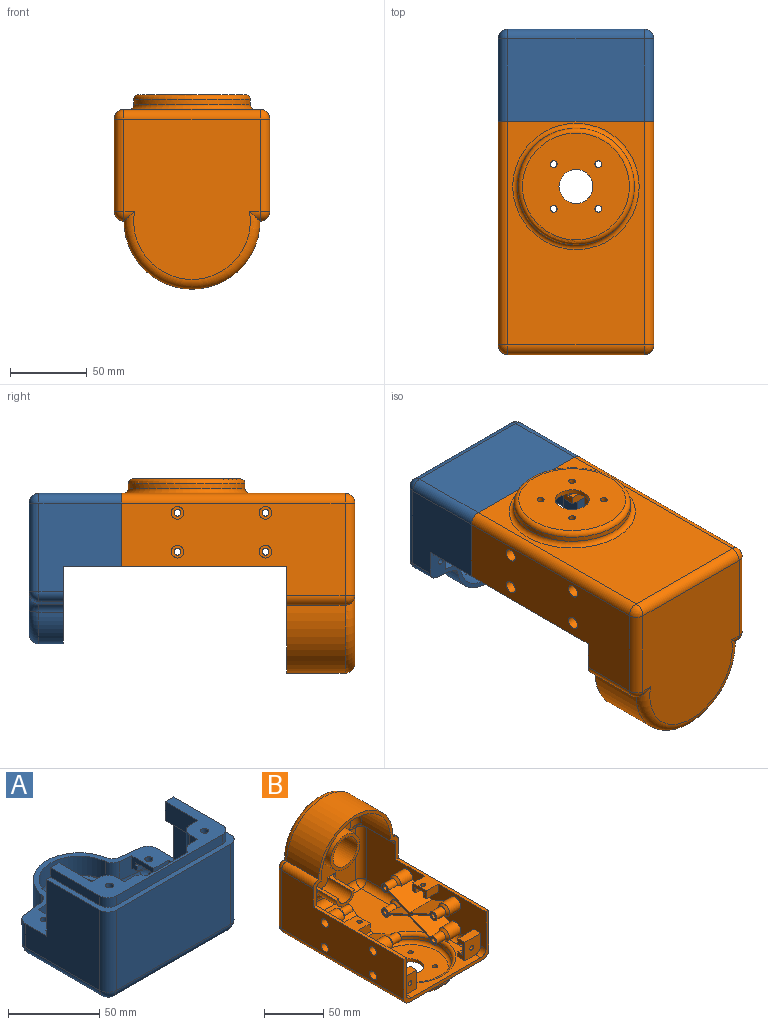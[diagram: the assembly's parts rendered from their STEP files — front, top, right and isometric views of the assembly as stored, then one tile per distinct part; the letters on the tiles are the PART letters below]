
ASSEMBLY  parts=2 mates=1
PART A: 121 faces, bbox 101.6x103.7x66.7 mm
  f0: plane 25.4x12.7mm, normal (1,0,0), area 322.6mm2, adj f10,f30,f31,f37
  f1: plane 12.7x6.55mm, normal (0,1,0), area 83.2mm2, adj f19,f31,f36,f119
  f2: plane 44.45x32.87mm, normal (-1,0,0), area 939.6mm2, adj f11,f20,f47,f58,f59,f103,f109,f112
  f3: plane 44.45x32.87mm, normal (1,0,0), area 939.6mm2, adj f10,f30,f47,f48,f51,f94,f99,f100
  f4: plane 8.89x1.27mm, normal (0,0,1), area 11.3mm2, adj f54,f56,f57,f62
  f5: plane 8.89x1.27mm, normal (0,0,1), area 11.3mm2, adj f54,f55,f56,f63
  f6: plane 8.89x1.27mm, normal (0,0,1), area 11.3mm2, adj f49,f50,f53,f60
  f7: plane 8.89x1.27mm, normal (0,0,1), area 11.3mm2, adj f50,f52,f53,f61
  f8: plane 14.41x12.7mm, normal (-0.12,-0.99,0), area 135.7mm2, adj f47,f54,f59,f110,f112,f117
  f9: plane 14.41x12.7mm, normal (0.12,-0.99,0), area 135.7mm2, adj f47,f48,f50,f100,f105,f115
  f10: plane 44.45x9.53mm, normal (0,1,0), area 201.6mm2, adj f0,f3,f12,f26,f28,f30,f31,f47
  f11: plane 44.45x9.53mm, normal (0,1,0), area 201.6mm2, adj f2,f15,f20,f26,f31,f32,f34,f47
  f12: plane 57.89x53.98mm, normal (-1,0,0), area 2491.7mm2, adj f10,f26,f47,f75,f81,f82
  f13: plane 82.55x54.33mm, normal (0,0,1), area 3316.7mm2, adj f87,f90,f92,f93,f98,f99,f101,f104
  f14: plane 88.9x85.73mm, normal (0,0,-1), area 6067.7mm2, adj f40,f42,f70,f73,f76,f77,f79,f82
  f15: plane 57.89x53.98mm, normal (1,0,0), area 2491.7mm2, adj f11,f26,f47,f68,f69,f70
  f16: cylinder r=2.22mm len=15.88mm, axis (0,0,1), area 221.7mm2, adj f31,f41
  f17: cylinder r=2.22mm len=15.88mm, axis (0,0,1), area 221.7mm2, adj f31,f39
  f18: plane 44.45x44.45mm, normal (0,1,0), area 1975.8mm2, adj f19,f86,f91,f92
  f19: plane 57.15x6.35mm, normal (0,0,-1), area 179.2mm2, adj f1,f18,f21,f33,f86,f91,f119,f120
  f20: plane 25.4x6.35mm, normal (0,0,-1), area 152.6mm2, adj f2,f11,f34,f103
  f21: plane 12.7x6.55mm, normal (0,1,0), area 83.2mm2, adj f19,f31,f38,f120
  f22: cylinder r=14.29mm len=28.58mm, axis (0,0,-1), area 855.1mm2, adj f24,f25
  f23: cylinder r=17.46mm len=34.93mm, axis (0,0,-1), area 348.4mm2, adj f24,f107
  f24: plane 34.93x34.93mm, normal (0,0,1), area 316.7mm2, adj f22,f23
  f25: plane 28.58x28.58mm, normal (0,0,1), area 641.3mm2, adj f22
  f26: plane 101.6x47.63mm, normal (0,0,1), area 604.8mm2, adj f10,f11,f12,f15,f27,f28,f29,f32
  f27: plane 88.9x53.98mm, normal (0,-1,0), area 4798.4mm2, adj f26,f69,f75,f76
  f28: plane 38.1x6.35mm, normal (-1,0,0), area 241.9mm2, adj f10,f26,f31,f114
  f29: plane 82.55x6.35mm, normal (0,-1,0), area 524.2mm2, adj f26,f31,f113,f114
  f30: plane 25.4x6.35mm, normal (0,0,-1), area 152.6mm2, adj f0,f3,f10,f94
  f31: plane 95.25x44.45mm, normal (0,0,1), area 1179.3mm2, adj f0,f1,f10,f11,f16,f17,f21,f28
  f32: plane 38.1x6.35mm, normal (1,0,0), area 241.9mm2, adj f11,f26,f31,f113
  f33: plane 31.75x12.7mm, normal (0,1,0), area 403.2mm2, adj f19,f31,f119,f120
  f34: plane 25.4x12.7mm, normal (-1,0,0), area 322.6mm2, adj f11,f20,f31,f35
  f35: plane 57.15x6.35mm, normal (0,1,0), area 362.9mm2, adj f31,f34,f97,f103,f104
  f36: plane 57.15x6.35mm, normal (-1,0,0), area 362.9mm2, adj f1,f31,f91,f97,f98
  f37: plane 57.15x6.35mm, normal (0,1,0), area 362.9mm2, adj f0,f31,f88,f93,f94
  f38: plane 57.15x6.35mm, normal (1,0,0), area 362.9mm2, adj f21,f31,f86,f87,f88
  f39: plane 8.26x8.26mm, normal (0,0,-1), area 38mm2, adj f17,f40
  f40: cylinder r=4.13mm len=50.8mm, axis (0,0,-1), area 1317.4mm2, adj f14,f39
  f41: plane 8.26x8.26mm, normal (0,0,-1), area 38mm2, adj f16,f42
  f42: cylinder r=4.13mm len=50.8mm, axis (0,0,-1), area 1317.4mm2, adj f14,f41
  f43: cylinder r=25.4mm len=49.98mm, axis (0,0,1), area 1122mm2, adj f47,f74,f79,f80
  f44: plane 15.88x14.79mm, normal (0.12,0.99,0), area 236.5mm2, adj f47,f68,f73,f74
  f45: plane 15.88x14.79mm, normal (-0.12,0.99,0), area 236.5mm2, adj f47,f80,f81,f85
  f46: cylinder r=22.23mm len=44.23mm, axis (0,0,-1), area 830.9mm2, adj f47,f108,f115,f117
  f47: plane 101.6x50.8mm, normal (0,0,1), area 868.3mm2, adj f2,f3,f8,f9,f10,f11,f12,f15
  f48: plane 17.04x11.43mm, normal (0,0,-1), area 101.1mm2, adj f3,f9,f49,f50,f51,f52,f53,f100
  f49: plane 8.89x3.3mm, normal (0,-1,0), area 29.4mm2, adj f6,f48,f50,f53
  f50: plane 17.04x8.26mm, normal (1,0,0), area 91mm2, adj f6,f7,f9,f47,f48,f49,f51,f52
  f51: plane 11.43x8.26mm, normal (0,-1,0), area 94.4mm2, adj f3,f47,f48,f50
  f52: plane 8.89x3.3mm, normal (0,1,0), area 29.4mm2, adj f7,f48,f50,f53
  f53: plane 11.43x5.08mm, normal (1,0,0), area 49.7mm2, adj f6,f7,f48,f49,f52,f60,f61,f65
  f54: plane 17.04x8.26mm, normal (-1,0,0), area 91mm2, adj f4,f5,f8,f47,f55,f57,f58,f59
  f55: plane 8.89x3.3mm, normal (0,-1,0), area 29.4mm2, adj f5,f54,f56,f59
  f56: plane 11.43x5.08mm, normal (-1,0,0), area 49.7mm2, adj f4,f5,f55,f57,f59,f62,f63,f67
  f57: plane 8.89x3.3mm, normal (0,1,0), area 29.4mm2, adj f4,f54,f56,f59
  f58: plane 11.43x8.26mm, normal (0,-1,0), area 94.4mm2, adj f2,f47,f54,f59
  f59: plane 17.04x11.43mm, normal (0,0,-1), area 101.1mm2, adj f2,f8,f54,f55,f56,f57,f58,f112
  f60: plane 8.89x1.78mm, normal (0,-1,0), area 15.8mm2, adj f6,f50,f53,f65
  f61: plane 8.89x1.78mm, normal (0,1,0), area 15.8mm2, adj f7,f50,f53,f65
  f62: plane 8.89x1.78mm, normal (0,1,0), area 15.8mm2, adj f4,f54,f56,f67
  f63: plane 8.89x1.78mm, normal (0,-1,0), area 15.8mm2, adj f5,f54,f56,f67
  f64: cylinder r=2.22mm len=4.45mm, axis (0,0,-1), area 44.3mm2, adj f47,f65
  f65: plane 11.43x8.89mm, normal (0,0,-1), area 86.1mm2, adj f50,f53,f60,f61,f64
  f66: cylinder r=2.22mm len=4.45mm, axis (0,0,-1), area 44.3mm2, adj f47,f67
  f67: plane 11.43x8.89mm, normal (0,0,-1), area 86.1mm2, adj f54,f56,f62,f63,f66
  f68: cylinder r=6.35mm len=15.88mm, axis (0,0,-1), area 145.8mm2, adj f15,f44,f47,f71
  f69: cylinder r=6.35mm len=53.98mm, axis (0,0,-1), area 538.4mm2, adj f15,f26,f27,f72
  f70: cylinder r=6.35mm len=57.89mm, axis (0,1,0), area 577.5mm2, adj f14,f15,f71,f72
  f71: sphere r=6.35mm, area 37.1mm2, adj f68,f70,f73
  f72: sphere r=6.35mm, area 63.3mm2, adj f69,f70,f76
  f73: cylinder r=6.35mm len=15.57mm, axis (0.99,-0.12,0), area 148.6mm2, adj f14,f44,f71,f77
  f74: cylinder r=6.35mm len=15.88mm, axis (0,0,1), area 127.7mm2, adj f43,f44,f47,f77
  f75: cylinder r=6.35mm len=53.98mm, axis (0,0,1), area 538.4mm2, adj f12,f26,f27,f78
  f76: cylinder r=6.35mm len=88.9mm, axis (-1,0,0), area 886.7mm2, adj f14,f27,f72,f78
  f77: torus R=12.7mm, axis (0,0,1), area 109.4mm2, adj f14,f73,f74,f79
  f78: sphere r=6.35mm, area 63.3mm2, adj f75,f76,f82
  f79: torus R=19.05mm, axis (0,0,1), area 640.9mm2, adj f14,f43,f77,f83
  f80: cylinder r=6.35mm len=15.88mm, axis (0,0,1), area 127.7mm2, adj f43,f45,f47,f83
  f81: cylinder r=6.35mm len=15.88mm, axis (0,0,-1), area 145.8mm2, adj f12,f45,f47,f84
  f82: cylinder r=6.35mm len=57.89mm, axis (0,-1,0), area 577.5mm2, adj f12,f14,f78,f84
  f83: torus R=12.7mm, axis (0,0,1), area 109.4mm2, adj f14,f79,f80,f85
  f84: sphere r=6.35mm, area 37.1mm2, adj f81,f82,f85
  f85: cylinder r=6.35mm len=15.57mm, axis (0.99,0.12,0), area 148.6mm2, adj f14,f45,f83,f84
  f86: cylinder r=6.35mm len=44.45mm, axis (0,0,1), area 443.4mm2, adj f18,f19,f38,f89
  f87: cylinder r=6.35mm len=6.35mm, axis (0,1,0), area 63.3mm2, adj f13,f38,f89,f90
  f88: cylinder r=6.35mm len=57.15mm, axis (0,0,1), area 570mm2, adj f31,f37,f38,f90
  f89: sphere r=6.35mm, area 63.3mm2, adj f86,f87,f92
  f90: torus R=12.7mm, axis (0,0,1), area 135.6mm2, adj f13,f87,f88,f93
  f91: cylinder r=6.35mm len=44.45mm, axis (0,0,-1), area 443.4mm2, adj f18,f19,f36,f95
  f92: cylinder r=6.35mm len=44.45mm, axis (1,0,0), area 443.4mm2, adj f13,f18,f89,f95
  f93: cylinder r=6.35mm len=6.35mm, axis (-1,0,0), area 63.3mm2, adj f13,f37,f90,f96
  f94: cylinder r=6.35mm len=44.45mm, axis (0,0,-1), area 443.4mm2, adj f3,f30,f37,f96
  f95: sphere r=6.35mm, area 40.3mm2, adj f91,f92,f98
  f96: sphere r=6.35mm, area 63.3mm2, adj f93,f94,f99
  f97: cylinder r=6.35mm len=57.15mm, axis (0,0,1), area 570mm2, adj f31,f35,f36,f101
  f98: cylinder r=6.35mm len=6.35mm, axis (0,-1,0), area 63.3mm2, adj f13,f36,f95,f101
  f99: cylinder r=6.35mm len=32.87mm, axis (0,1,0), area 327.8mm2, adj f3,f13,f96,f102
  f100: cylinder r=6.35mm len=6.3mm, axis (0,0,1), area 40.8mm2, adj f3,f9,f48,f102
  f101: torus R=12.7mm, axis (0,0,1), area 135.6mm2, adj f13,f97,f98,f104
  f102: sphere r=6.35mm, area 37.1mm2, adj f99,f100,f105
  f103: cylinder r=6.35mm len=44.45mm, axis (0,0,-1), area 443.4mm2, adj f2,f20,f35,f106
  f104: cylinder r=6.35mm len=6.35mm, axis (-1,0,0), area 63.3mm2, adj f13,f35,f101,f106
  f105: cylinder r=6.35mm len=22.09mm, axis (0.99,0.12,0), area 186mm2, adj f9,f13,f102,f107,f116
  f106: sphere r=6.35mm, area 86.4mm2, adj f103,f104,f109
  f107: torus R=23.81mm, axis (0,0,1), area 892.1mm2, adj f13,f23,f105,f108,f110,f116,f118
  f108: torus R=15.88mm, axis (0,0,1), area 370.4mm2, adj f46,f107,f116,f118
  f109: cylinder r=6.35mm len=32.87mm, axis (0,-1,0), area 327.8mm2, adj f2,f13,f106,f111
  f110: cylinder r=6.35mm len=22.09mm, axis (0.99,-0.12,0), area 186mm2, adj f8,f13,f107,f111,f118
  f111: sphere r=6.35mm, area 60.1mm2, adj f109,f110,f112
  f112: cylinder r=6.35mm len=6.3mm, axis (0,0,1), area 40.8mm2, adj f2,f8,f59,f111
  f113: cylinder r=6.35mm len=6.35mm, axis (0,0,-1), area 63.3mm2, adj f26,f29,f31,f32
  f114: cylinder r=6.35mm len=6.35mm, axis (0,0,1), area 63.3mm2, adj f26,f28,f29,f31
  f115: cylinder r=6.35mm len=12.7mm, axis (0,0,-1), area 108.7mm2, adj f9,f46,f47,f116
  f116: bspline ~9.93x8.8mm, area 52mm2, adj f105,f107,f108,f115
  f117: cylinder r=6.35mm len=12.7mm, axis (0,0,-1), area 108.7mm2, adj f8,f46,f47,f118
  f118: bspline ~10.23x8.96mm, area 52mm2, adj f107,f108,f110,f117
  f119: cylinder r=6.35mm len=12.7mm, axis (0,0,1), area 106.3mm2, adj f1,f19,f31,f33
  f120: cylinder r=6.35mm len=12.7mm, axis (0,0,1), area 106.3mm2, adj f19,f21,f31,f33
PART B: 195 faces, bbox 101.8x154.7x130.8 mm
  f0: cylinder r=2.22mm len=4.45mm, axis (0,0,1), area 44.3mm2, adj f187,f188
  f1: cylinder r=2.22mm len=4.45mm, axis (0,0,1), area 44.3mm2, adj f187,f188
  f2: cylinder r=2.22mm len=4.45mm, axis (0,0,1), area 44.3mm2, adj f187,f188
  f3: cylinder r=2.22mm len=4.45mm, axis (0,0,1), area 44.3mm2, adj f187,f188
  f4: cylinder r=11.11mm len=22.23mm, axis (0,0,-1), area 221.7mm2, adj f187,f188
  f5: plane 46.53x14.14mm, normal (-1,0,0), area 413.9mm2, adj f25,f30,f77,f79,f170
  f6: plane 142.88x53.98mm, normal (1,0,0), area 4724.8mm2, adj f9,f19,f38,f39,f41,f42,f43,f44
  f7: plane 19.05x8.26mm, normal (-1,0,0), area 107.6mm2, adj f17,f45,f105,f106,f109,f110,f115,f116
  f8: plane 11.43x5.08mm, normal (-1,0,0), area 49.7mm2, adj f17,f109,f110,f115,f116,f117,f118,f153
  f9: plane 19.05x8.26mm, normal (0,0,1), area 157.3mm2, adj f6,f102,f104,f152
  f10: plane 11.43x5.08mm, normal (1,0,0), area 49.7mm2, adj f103,f107,f108,f111,f112,f113,f114,f152
  f11: plane 46.53x14.14mm, normal (1,0,0), area 413.9mm2, adj f37,f40,f55,f56,f175
  f12: plane 142.88x53.98mm, normal (-1,0,0), area 4724.8mm2, adj f20,f26,f27,f28,f29,f31,f32,f70
  f13: plane 146.05x60.33mm, normal (-1,0,0), area 6539.9mm2, adj f19,f58,f60,f62,f64,f101,f125,f158
  f14: plane 104.78x88.9mm, normal (0,1,0), area 8124.7mm2, adj f156,f159,f162,f164,f165,f167
  f15: plane 146.05x60.33mm, normal (1,0,0), area 6539.9mm2, adj f20,f81,f83,f85,f87,f101,f125,f154
  f16: plane 98.43x82.55mm, normal (0,-1,0), area 4867.2mm2, adj f96,f97,f99,f169,f173,f174,f176,f178
  f17: plane 13.97x11.43mm, normal (0,1,0), area 144.2mm2, adj f7,f8,f109,f110,f119
  f18: plane 146.05x88.9mm, normal (0,0,-1), area 7631.7mm2, adj f101,f154,f158,f159,f192
  f19: plane 107.95x17.15mm, normal (0,0,1), area 557.9mm2, adj f6,f13,f101,f125,f126,f127,f129,f150
  f20: plane 107.95x17.15mm, normal (0,0,1), area 557.9mm2, adj f12,f15,f101,f125,f130,f132,f133,f151
  f21: cylinder r=2.22mm len=16.89mm, axis (1,0,0), area 235.9mm2, adj f75,f86
  f22: cylinder r=2.22mm len=16.89mm, axis (1,0,0), area 235.9mm2, adj f75,f84
  f23: cylinder r=2.22mm len=16.99mm, axis (1,0,0), area 237.3mm2, adj f82,f194
  f24: cylinder r=2.22mm len=16.89mm, axis (1,0,0), area 235.9mm2, adj f75,f80
  f25: plane 26.58x24.8mm, normal (0,0.4,-0.91), area 676.9mm2, adj f5,f30,f72,f75,f79,f91
  f26: plane 26.42x23.02mm, normal (0,-0.4,0.91), area 632mm2, adj f12,f72,f73,f75,f79,f91
  f27: plane 26.42x23.02mm, normal (0,-0.4,-0.91), area 632mm2, adj f12,f73,f74,f75,f78,f90
  f28: plane 26.58x24.8mm, normal (0,0.4,0.91), area 676.9mm2, adj f12,f32,f74,f75,f78,f90
  f29: plane 26.42x23.02mm, normal (0,0.4,0.91), area 632mm2, adj f12,f70,f71,f75,f77,f88
  f30: plane 26.58x24.8mm, normal (0,-0.4,-0.91), area 676.9mm2, adj f5,f25,f71,f75,f77,f88
  f31: plane 26.42x23.02mm, normal (0,0.4,-0.91), area 632mm2, adj f12,f69,f70,f75,f76,f89
  f32: plane 26.58x24.8mm, normal (0,-0.4,0.91), area 676.9mm2, adj f12,f28,f69,f75,f76,f89
  f33: cylinder r=2.22mm len=16.89mm, axis (1,0,0), area 235.9mm2, adj f52,f63
  f34: cylinder r=2.22mm len=16.89mm, axis (1,0,0), area 235.9mm2, adj f52,f61
  f35: cylinder r=2.22mm len=16.89mm, axis (1,0,0), area 235.9mm2, adj f52,f59
  f36: cylinder r=2.22mm len=16.89mm, axis (1,0,0), area 235.9mm2, adj f52,f57
  f37: plane 26.58x24.8mm, normal (0,-0.4,-0.91), area 676.9mm2, adj f11,f40,f51,f52,f56,f65
  f38: plane 26.42x23.02mm, normal (0,0.4,0.91), area 632mm2, adj f6,f46,f51,f52,f56,f65
  f39: plane 26.42x23.02mm, normal (0,-0.4,0.91), area 632mm2, adj f6,f49,f50,f52,f55,f66
  f40: plane 26.58x24.8mm, normal (0,0.4,-0.91), area 676.9mm2, adj f11,f37,f50,f52,f55,f66
  f41: plane 26.42x23.02mm, normal (0,0.4,-0.91), area 632mm2, adj f6,f46,f47,f52,f54,f68
  f42: plane 26.58x24.8mm, normal (0,-0.4,0.91), area 676.9mm2, adj f6,f43,f47,f52,f54,f68
  f43: plane 26.58x24.8mm, normal (0,0.4,0.91), area 676.9mm2, adj f6,f42,f48,f52,f53,f67
  f44: plane 26.42x23.02mm, normal (0,-0.4,-0.91), area 632mm2, adj f6,f48,f49,f52,f53,f67
  f45: plane 142.88x82.55mm, normal (0,0,1), area 7024.3mm2, adj f7,f101,f102,f104,f105,f152,f153,f170
  f46: plane 26.42x1.74mm, normal (0,1,0), area 45.8mm2, adj f6,f38,f41,f52
  f47: cylinder r=4.13mm len=10.54mm, axis (-1,0,0), area 256.2mm2, adj f41,f42,f52,f68
  f48: cylinder r=4.13mm len=10.54mm, axis (-1,0,0), area 256.2mm2, adj f43,f44,f52,f67
  f49: plane 26.42x1.74mm, normal (0,-1,0), area 45.8mm2, adj f6,f39,f44,f52
  f50: cylinder r=4.13mm len=10.54mm, axis (-1,0,0), area 256.2mm2, adj f39,f40,f52,f66
  f51: cylinder r=4.13mm len=10.54mm, axis (-1,0,0), area 256.2mm2, adj f37,f38,f52,f65
  f52: plane 65.79x33.66mm, normal (1,0,0), area 327.3mm2, adj f33,f34,f35,f36,f37,f38,f39,f40
  f53: cylinder r=6.35mm len=13.65mm, axis (-1,0,0), area 522.8mm2, adj f6,f43,f44,f67
  f54: cylinder r=6.35mm len=13.65mm, axis (-1,0,0), area 522.8mm2, adj f6,f41,f42,f68
  f55: cylinder r=6.35mm len=13.65mm, axis (-1,0,0), area 517mm2, adj f6,f11,f39,f40,f66,f175
  f56: cylinder r=6.35mm len=13.65mm, axis (-1,0,0), area 517mm2, adj f6,f11,f37,f38,f65,f175
  f57: plane 8.26x8.26mm, normal (-1,0,0), area 38mm2, adj f36,f58
  f58: cylinder r=4.13mm len=12.7mm, axis (-1,0,0), area 329.4mm2, adj f13,f57
  f59: plane 8.26x8.26mm, normal (-1,0,0), area 38mm2, adj f35,f60
  f60: cylinder r=4.13mm len=12.7mm, axis (-1,0,0), area 329.4mm2, adj f13,f59
  f61: plane 8.26x8.26mm, normal (-1,0,0), area 38mm2, adj f34,f62
  f62: cylinder r=4.13mm len=12.7mm, axis (-1,0,0), area 329.4mm2, adj f13,f61
  f63: plane 8.26x8.26mm, normal (-1,0,0), area 38mm2, adj f33,f64
  f64: cylinder r=4.13mm len=12.7mm, axis (-1,0,0), area 329.4mm2, adj f13,f63
  f65: cone r=4.13mm half-angle=45deg, axis (-1,0,0), area 98.2mm2, adj f37,f38,f51,f56
  f66: cone r=4.13mm half-angle=45deg, axis (-1,0,0), area 98.2mm2, adj f39,f40,f50,f55
  f67: cone r=4.13mm half-angle=45deg, axis (-1,0,0), area 98.2mm2, adj f43,f44,f48,f53
  f68: cone r=4.13mm half-angle=45deg, axis (-1,0,0), area 98.2mm2, adj f41,f42,f47,f54
  f69: cylinder r=4.13mm len=10.64mm, axis (1,0,0), area 258.8mm2, adj f31,f32,f75,f89,f194
  f70: plane 26.42x1.74mm, normal (0,1,0), area 45.8mm2, adj f12,f29,f31,f75
  f71: cylinder r=4.13mm len=10.54mm, axis (1,0,0), area 256.2mm2, adj f29,f30,f75,f88
  f72: cylinder r=4.13mm len=10.54mm, axis (1,0,0), area 256.2mm2, adj f25,f26,f75,f91
  f73: plane 26.42x1.74mm, normal (0,-1,0), area 45.8mm2, adj f12,f26,f27,f75
  f74: cylinder r=4.13mm len=10.54mm, axis (1,0,0), area 256.2mm2, adj f27,f28,f75,f90
  f75: plane 65.79x33.66mm, normal (-1,0,0), area 289.3mm2, adj f21,f22,f24,f25,f26,f27,f28,f29
  f76: cylinder r=6.35mm len=13.65mm, axis (1,0,0), area 522.8mm2, adj f12,f31,f32,f89
  f77: cylinder r=6.35mm len=13.65mm, axis (1,0,0), area 517mm2, adj f5,f12,f29,f30,f88,f170
  f78: cylinder r=6.35mm len=13.65mm, axis (1,0,0), area 522.8mm2, adj f12,f27,f28,f90
  f79: cylinder r=6.35mm len=13.65mm, axis (1,0,0), area 517mm2, adj f5,f12,f25,f26,f91,f170
  f80: plane 8.26x8.26mm, normal (1,0,0), area 38mm2, adj f24,f81
  f81: cylinder r=4.13mm len=12.7mm, axis (1,0,0), area 329.4mm2, adj f15,f80
  f82: plane 8.26x8.26mm, normal (1,0,0), area 38mm2, adj f23,f83
  f83: cylinder r=4.13mm len=12.7mm, axis (1,0,0), area 329.4mm2, adj f15,f82
  f84: plane 8.26x8.26mm, normal (1,0,0), area 38mm2, adj f22,f85
  f85: cylinder r=4.13mm len=12.7mm, axis (1,0,0), area 329.4mm2, adj f15,f84
  f86: plane 8.26x8.26mm, normal (1,0,0), area 38mm2, adj f21,f87
  f87: cylinder r=4.13mm len=12.7mm, axis (1,0,0), area 329.4mm2, adj f15,f86
  f88: cone r=4.13mm half-angle=45deg, axis (1,0,0), area 98.2mm2, adj f29,f30,f71,f77
  f89: cone r=4.13mm half-angle=45deg, axis (1,0,0), area 98.2mm2, adj f31,f32,f69,f76
  f90: cone r=4.13mm half-angle=45deg, axis (1,0,0), area 98.2mm2, adj f27,f28,f74,f78
  f91: cone r=4.13mm half-angle=45deg, axis (1,0,0), area 98.2mm2, adj f25,f26,f72,f79
  f92: cylinder r=14.29mm len=28.58mm, axis (0,1,0), area 2565.2mm2, adj f94,f95
  f93: cylinder r=17.46mm len=34.93mm, axis (0,1,0), area 2438.5mm2, adj f94,f183
  f94: plane 34.93x34.93mm, normal (0,-1,0), area 316.7mm2, adj f92,f93
  f95: plane 28.58x28.58mm, normal (0,-1,0), area 641.3mm2, adj f92
  f96: cylinder r=7.94mm len=28.58mm, axis (0,1,0), area 712.6mm2, adj f16,f97,f99,f100
  f97: plane 28.58x9.53mm, normal (0,0,1), area 99.4mm2, adj f16,f96,f98,f100,f182
  f98: cylinder r=11.11mm len=22.23mm, axis (0,1,0), area 775.9mm2, adj f97,f99,f100,f182
  f99: plane 28.58x9.53mm, normal (0,0,1), area 99.4mm2, adj f16,f96,f98,f100,f182
  f100: plane 22.23x11.11mm, normal (0,-1,0), area 95mm2, adj f96,f97,f98,f99
  f101: plane 101.6x47.63mm, normal (0,-1,0), area 604.8mm2, adj f6,f12,f13,f15,f18,f19,f20,f45
  f102: plane 19.05x19.05mm, normal (0,-1,0), area 338.7mm2, adj f6,f9,f45,f104,f120,f184
  f103: plane 13.97x11.43mm, normal (0,1,0), area 144.2mm2, adj f10,f104,f107,f108,f120
  f104: plane 19.05x8.26mm, normal (1,0,0), area 107.6mm2, adj f9,f45,f102,f103,f107,f108,f111,f112
  f105: plane 19.05x19.05mm, normal (0,-1,0), area 338.7mm2, adj f7,f12,f45,f106,f119,f185
  f106: plane 19.05x8.26mm, normal (0,0,1), area 157.3mm2, adj f7,f12,f105,f153
  f107: plane 13.97x1.78mm, normal (0,0,-1), area 24.8mm2, adj f10,f103,f104,f111
  f108: plane 13.97x1.78mm, normal (0,0,1), area 24.8mm2, adj f10,f103,f104,f114
  f109: plane 13.97x1.78mm, normal (0,0,-1), area 24.8mm2, adj f7,f8,f17,f118
  f110: plane 13.97x1.78mm, normal (0,0,1), area 24.8mm2, adj f7,f8,f17,f115
  f111: plane 13.97x1.27mm, normal (0,-1,0), area 17.7mm2, adj f10,f104,f107,f112
  f112: plane 13.97x3.3mm, normal (0,0,-1), area 46.1mm2, adj f10,f104,f111,f152
  f113: plane 13.97x3.3mm, normal (0,0,1), area 46.1mm2, adj f10,f104,f114,f152
  f114: plane 13.97x1.27mm, normal (0,-1,0), area 17.7mm2, adj f10,f104,f108,f113
  f115: plane 13.97x1.27mm, normal (0,-1,0), area 17.7mm2, adj f7,f8,f110,f117
  f116: plane 13.97x3.3mm, normal (0,0,-1), area 46.1mm2, adj f7,f8,f118,f153
  f117: plane 13.97x3.3mm, normal (0,0,1), area 46.1mm2, adj f7,f8,f115,f153
  f118: plane 13.97x1.27mm, normal (0,-1,0), area 17.7mm2, adj f7,f8,f109,f116
  f119: cylinder r=2.22mm len=4.45mm, axis (0,-1,0), area 44.3mm2, adj f17,f105
  f120: cylinder r=2.22mm len=4.45mm, axis (0,-1,0), area 44.3mm2, adj f102,f103
  f121: cylinder r=44.45mm len=88.9mm, axis (0,1,0), area 5320.4mm2, adj f125,f157,f163,f165
  f122: plane 34.93x0.12mm, normal (0,0,-1), area 4.3mm2, adj f123,f125,f178,f181
  f123: cylinder r=41.27mm len=82.55mm, axis (0,1,0), area 4750.7mm2, adj f122,f124,f125,f176
  f124: plane 34.93x0.12mm, normal (0,0,-1), area 4.3mm2, adj f123,f125,f168,f173
  f125: plane 101.6x69.85mm, normal (0,-1,0), area 629.4mm2, adj f6,f12,f13,f15,f19,f20,f121,f122
  f126: plane 13.97x8.26mm, normal (0,1,0), area 115.3mm2, adj f6,f19,f129,f141
  f127: plane 13.97x8.26mm, normal (0,-1,0), area 115.3mm2, adj f6,f19,f129,f141
  f128: plane 11.43x8.89mm, normal (0,0,-1), area 86.1mm2, adj f129,f134,f135,f136,f150
  f129: plane 16.51x8.26mm, normal (1,0,0), area 86.6mm2, adj f19,f126,f127,f128,f134,f136,f137,f138
  f130: plane 13.97x8.26mm, normal (0,1,0), area 115.3mm2, adj f12,f20,f133,f148
  f131: plane 11.43x11.43mm, normal (0,0,-1), area 115.1mm2, adj f133,f142,f143,f144,f151
  f132: plane 13.97x8.26mm, normal (0,-1,0), area 115.3mm2, adj f12,f20,f133,f148
  f133: plane 16.51x8.26mm, normal (-1,0,0), area 86.6mm2, adj f20,f130,f131,f132,f142,f144,f145,f146
  f134: plane 8.89x1.78mm, normal (0,-1,0), area 15.8mm2, adj f128,f129,f135,f138
  f135: plane 11.43x5.08mm, normal (1,0,0), area 49.7mm2, adj f128,f134,f136,f137,f138,f139,f140,f141
  f136: plane 8.89x1.78mm, normal (0,1,0), area 15.8mm2, adj f128,f129,f135,f137
  f137: plane 8.89x1.27mm, normal (0,0,1), area 11.3mm2, adj f129,f135,f136,f140
  f138: plane 8.89x1.27mm, normal (0,0,1), area 11.3mm2, adj f129,f134,f135,f139
  f139: plane 8.89x3.3mm, normal (0,-1,0), area 29.4mm2, adj f129,f135,f138,f141
  f140: plane 8.89x3.3mm, normal (0,1,0), area 29.4mm2, adj f129,f135,f137,f141
  f141: plane 16.51x13.97mm, normal (0,0,-1), area 151.6mm2, adj f6,f126,f127,f129,f135,f139,f140
  f142: plane 11.43x1.78mm, normal (0,1,0), area 20.3mm2, adj f131,f133,f143,f145
  f143: plane 11.43x5.08mm, normal (-1,0,0), area 49.7mm2, adj f131,f142,f144,f145,f146,f147,f148,f149
  f144: plane 11.43x1.78mm, normal (0,-1,0), area 20.3mm2, adj f131,f133,f143,f149
  f145: plane 11.43x1.27mm, normal (0,0,1), area 14.5mm2, adj f133,f142,f143,f147
  f146: plane 11.43x3.3mm, normal (0,-1,0), area 37.7mm2, adj f133,f143,f148,f149
  f147: plane 11.43x3.3mm, normal (0,1,0), area 37.7mm2, adj f133,f143,f145,f148
  f148: plane 16.51x13.97mm, normal (0,0,-1), area 129mm2, adj f12,f130,f132,f133,f143,f146,f147
  f149: plane 11.43x1.27mm, normal (0,0,1), area 14.5mm2, adj f133,f143,f144,f146
  f150: cylinder r=2.22mm len=4.45mm, axis (0,0,1), area 44.3mm2, adj f19,f128
  f151: cylinder r=2.22mm len=4.45mm, axis (0,0,1), area 44.3mm2, adj f20,f131
  f152: plane 19.05x19.05mm, normal (0,1,0), area 230.1mm2, adj f6,f9,f10,f45,f104,f112,f113,f175
  f153: plane 19.05x19.05mm, normal (0,1,0), area 230.1mm2, adj f7,f8,f12,f45,f106,f116,f117,f170
  f154: cylinder r=6.35mm len=146.05mm, axis (0,1,0), area 1456.8mm2, adj f15,f18,f101,f155
  f155: sphere r=6.35mm, area 63.3mm2, adj f154,f156,f159
  f156: cylinder r=6.35mm len=60.33mm, axis (0,0,-1), area 601.7mm2, adj f14,f15,f155,f160
  f157: cylinder r=6.35mm len=38.1mm, axis (0,1,0), area 380mm2, adj f15,f121,f125,f160
  f158: cylinder r=6.35mm len=146.05mm, axis (0,-1,0), area 1456.8mm2, adj f13,f18,f101,f161
  f159: cylinder r=6.35mm len=88.9mm, axis (-1,0,0), area 886.7mm2, adj f14,f18,f155,f161
  f160: sphere r=6.35mm, area 63.3mm2, adj f156,f157,f162
  f161: sphere r=6.35mm, area 63.3mm2, adj f158,f159,f164
  f162: cylinder r=6.35mm len=6.88mm, axis (-1,0,0), area 24.2mm2, adj f14,f160,f165
  f163: cylinder r=6.35mm len=38.1mm, axis (0,-1,0), area 380mm2, adj f13,f121,f125,f166
  f164: cylinder r=6.35mm len=60.33mm, axis (0,0,1), area 601.7mm2, adj f13,f14,f161,f166
  f165: torus R=38.1mm, axis (0,1,0), area 1366.7mm2, adj f14,f121,f162,f167
  f166: sphere r=6.35mm, area 63.3mm2, adj f163,f164,f167
  f167: cylinder r=6.35mm len=6.88mm, axis (-1,0,0), area 24.2mm2, adj f14,f165,f166
  f168: cylinder r=6.35mm len=34.93mm, axis (0,1,0), area 348.4mm2, adj f12,f124,f125,f171
  f169: cylinder r=6.35mm len=53.98mm, axis (0,0,1), area 538.4mm2, adj f12,f16,f171,f172
  f170: cylinder r=6.35mm len=128.27mm, axis (0,-1,0), area 1228.3mm2, adj f5,f12,f45,f77,f79,f153,f172
  f171: sphere r=6.35mm, area 63.3mm2, adj f168,f169,f173
  f172: sphere r=6.35mm, area 63.3mm2, adj f169,f170,f174
  f173: cylinder r=6.35mm len=7.67mm, axis (1,0,0), area 27.6mm2, adj f16,f124,f171,f176
  f174: cylinder r=6.35mm len=82.55mm, axis (1,0,0), area 823.4mm2, adj f16,f45,f172,f177
  f175: cylinder r=6.35mm len=128.27mm, axis (0,1,0), area 1228.3mm2, adj f6,f11,f45,f55,f56,f152,f177
  f176: torus R=34.92mm, axis (0,-1,0), area 1331mm2, adj f16,f123,f173,f178
  f177: sphere r=6.35mm, area 63.3mm2, adj f174,f175,f179
  f178: cylinder r=6.35mm len=7.67mm, axis (1,0,0), area 27.6mm2, adj f16,f122,f176,f180
  f179: cylinder r=6.35mm len=53.98mm, axis (0,0,-1), area 538.4mm2, adj f6,f16,f177,f180
  f180: sphere r=6.35mm, area 63.3mm2, adj f178,f179,f181
  f181: cylinder r=6.35mm len=34.93mm, axis (0,-1,0), area 348.4mm2, adj f6,f122,f125,f180
  f182: torus R=17.46mm, axis (0,-1,0), area 420.5mm2, adj f16,f97,f98,f99
  f183: torus R=23.81mm, axis (0,-1,0), area 1239mm2, adj f16,f93
  f184: cylinder r=6.35mm len=6.35mm, axis (0,1,0), area 63.3mm2, adj f6,f45,f101,f102
  f185: cylinder r=6.35mm len=6.35mm, axis (0,-1,0), area 63.3mm2, adj f12,f45,f101,f105
  f186: cylinder r=38.1mm len=76.2mm, axis (0,0,1), area 760.1mm2, adj f192,f193
  f187: plane 69.85x69.85mm, normal (0,0,-1), area 3382mm2, adj f0,f1,f2,f3,f4,f193
  f188: plane 63.5x63.5mm, normal (0,0,1), area 2716.9mm2, adj f0,f1,f2,f3,f4,f191
  f189: cylinder r=34.92mm len=69.85mm, axis (0,0,1), area 696.7mm2, adj f190,f191
  f190: torus R=38.1mm, axis (0,0,1), area 1130.6mm2, adj f45,f189
  f191: torus R=31.75mm, axis (0,0,1), area 1058.3mm2, adj f188,f189
  f192: torus R=41.27mm, axis (0,0,1), area 1230.1mm2, adj f18,f186
  f193: torus R=34.92mm, axis (0,0,-1), area 1157.7mm2, adj f186,f187
  f194: plane 8.26x8.26mm, normal (-1,0,0), area 38mm2, adj f23,f69
PLACE A rot(axis=(0,0.71,-0.71),180deg) t=(0,73.02,0)mm
PLACE B rot(axis=(1,0,0),180deg) t=(0,-46.74,73.02)mm
MATE fastened A.f29 <-> B.f45  axis (0,0,1) through (0,12.7,69.85)mm
